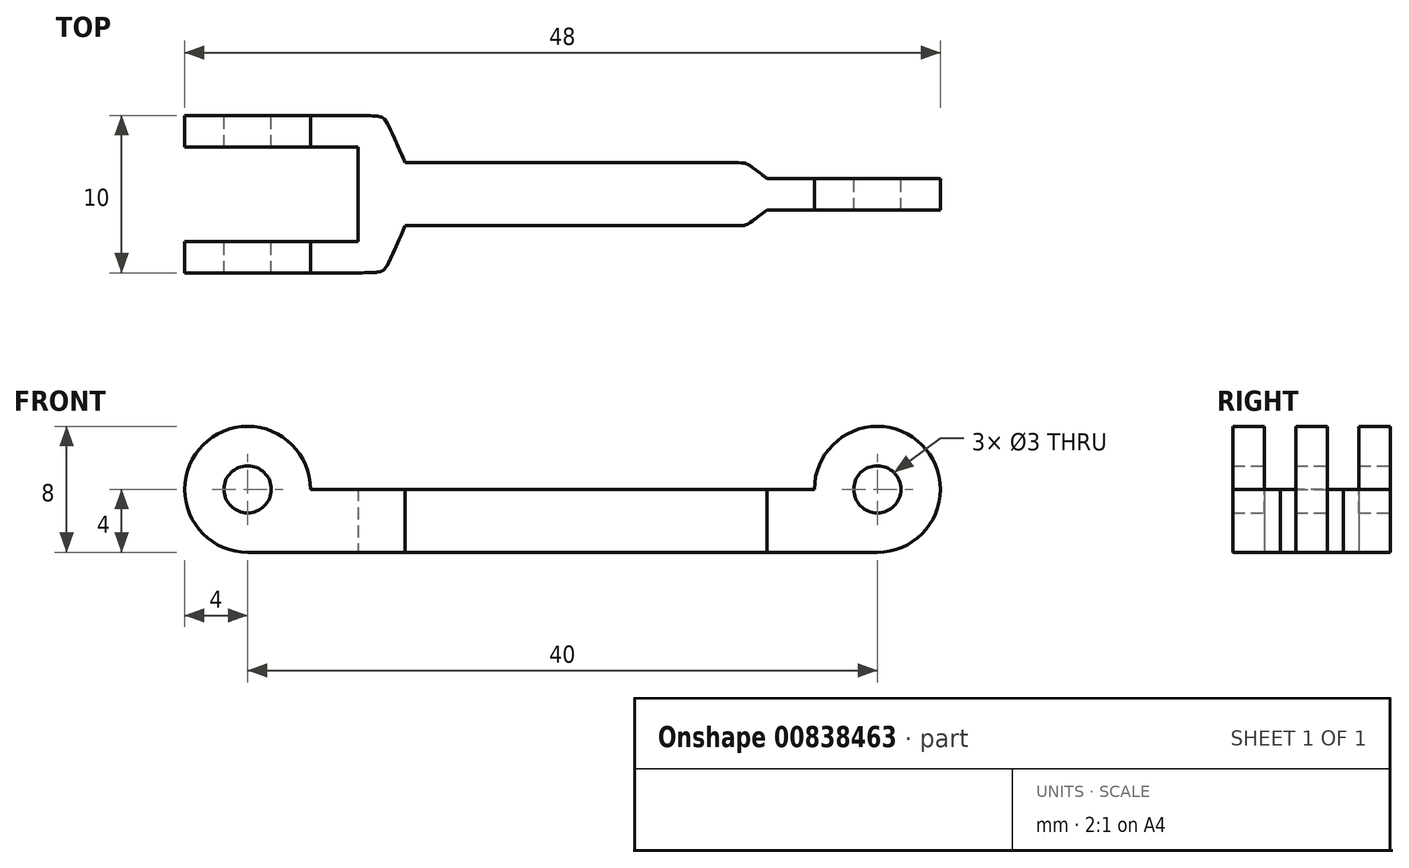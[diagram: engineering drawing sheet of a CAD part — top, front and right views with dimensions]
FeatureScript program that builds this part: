
annotation { "Feature Type Name" : "Feature", "Feature Type Description" : "" }
export const myFeature = defineFeature(function(context is Context, id is Id, definition is map)
    precondition{}
    {
        {
            var Q0;
            Q0=qCreatedBy(makeId("Front.planeOp"),FACE);
            var sketch = newSketch(context, id + "F0", { "sketchPlane" : qUnion([Q0])});
            skLineSegment(sketch, "E0.bottom", {"start": v(20, 2) * mm, "end": v(-20, 2) * mm});
            skLineSegment(sketch, "E0.top", {"start": v(20, -2) * mm, "end": v(-20, -2) * mm});
            skLineSegment(sketch, "E0.left", {"start": v(20, 2) * mm, "end": v(20, -2) * mm});
            skLineSegment(sketch, "E0.right", {"start": v(-20, 2) * mm, "end": v(-20, -2) * mm});
            skPoint(sketch, "E0.middle", {"position": v(0, 0) * mm});
            skLineSegment(sketch, "E1", {"start": v(-13, 2) * mm, "end": v(-13, -2) * mm});
            skLineSegment(sketch, "E2", {"start": v(-10, 2) * mm, "end": v(-10, -2) * mm});
            skCircle(sketch, "E3", {"center": v(20, 2) * mm, "radius": 4 * mm});
            skCircle(sketch, "E4", {"center": v(-20, 2) * mm, "radius": 4 * mm});
            skCircle(sketch, "E5", {"center": v(20, 2) * mm, "radius": 1.5 * mm});
            skCircle(sketch, "E6", {"center": v(-20, 2) * mm, "radius": 1.5 * mm});
            skLineSegment(sketch, "E7", {"start": v(13, 2) * mm, "end": v(13, -2) * mm});
            skSolve(sketch);
        }
        {
            var Q0;
            {var subQ0=sQuery(id+"F0.wireOp",EDGE,"E4");var subQ1=sQuery(id+"F0.wireOp",EDGE,"E0.bottom");var subQ2=makeQuery(id+"F0.imprint","INTERSECT",VERTEX,{"derivedFrom":[subQ1,subQ0]});Q0=makeQuery(id+"F0.imprint","IMPRINT",FACE,{"disambiguationData":[TD([[makeQuery(id+"F0.imprint","IMPRINT",EDGE,{"disambiguationData":[TD([[subQ2,-1.0]])],"derivedFrom":subQ1}),-1.0]])]});}
            var Q1;
            {var subQ0=sQuery(id+"F0.wireOp",EDGE,"E4");var subQ1=sQuery(id+"F0.wireOp",EDGE,"E0.bottom");var subQ2=makeQuery(id+"F0.imprint","INTERSECT",VERTEX,{"derivedFrom":[subQ1,subQ0]});Q1=makeQuery(id+"F0.imprint","IMPRINT",FACE,{"disambiguationData":[TD([[makeQuery(id+"F0.imprint","IMPRINT",EDGE,{"disambiguationData":[TD([[subQ2,-1.0]])],"derivedFrom":subQ1}),1.0]])]});}
            var Q2;
            {var subQ0=sQuery(id+"F0.wireOp",EDGE,"E1");Q2=makeQuery(id+"F0.imprint","IMPRINT",FACE,{"disambiguationData":[TD([[makeQuery(id+"F0.imprint","IMPRINT",EDGE,{"derivedFrom":subQ0}),-1.0]])]});}
            var Q3;
            {var subQ0=sQuery(id+"F0.wireOp",EDGE,"E1");Q3=makeQuery(id+"F0.imprint","IMPRINT",FACE,{"disambiguationData":[TD([[makeQuery(id+"F0.imprint","IMPRINT",EDGE,{"derivedFrom":subQ0}),1.0]])]});}
            extrude(context, id + "F1", {"entities" : qUnion([Q0, Q1, Q2, Q3]), "depth" : 10 * mm, "offsetDistance" : 25 * mm, "symmetric" : true});
        }
        {
            var Q0;
            {var subQ0=sQuery(id+"F0.wireOp",EDGE,"E2");Q0=makeQuery(id+"F0.imprint","IMPRINT",FACE,{"disambiguationData":[TD([[makeQuery(id+"F0.imprint","IMPRINT",EDGE,{"derivedFrom":subQ0}),1.0]])]});}
            extrude(context, id + "F2", {"entities" : qUnion([Q0]), "operationType" : NewBodyOperationType.ADD, "depth" : 4 * mm, "offsetDistance" : 25 * mm, "symmetric" : true});
        }
        {
            var Q0;
            {var subQ0=sQuery(id+"F0.wireOp",EDGE,"E7");Q0=makeQuery(id+"F0.imprint","IMPRINT",FACE,{"disambiguationData":[TD([[makeQuery(id+"F0.imprint","IMPRINT",EDGE,{"derivedFrom":subQ0}),1.0]])]});}
            var Q1;
            {var subQ0=sQuery(id+"F0.wireOp",EDGE,"E3");var subQ1=sQuery(id+"F0.wireOp",EDGE,"E0.bottom");var subQ2=makeQuery(id+"F0.imprint","INTERSECT",VERTEX,{"derivedFrom":[subQ1,subQ0]});Q1=makeQuery(id+"F0.imprint","IMPRINT",FACE,{"disambiguationData":[TD([[makeQuery(id+"F0.imprint","IMPRINT",EDGE,{"disambiguationData":[TD([[subQ2,1.0]])],"derivedFrom":subQ1}),1.0]])]});}
            var Q2;
            {var subQ0=sQuery(id+"F0.wireOp",EDGE,"E3");var subQ1=sQuery(id+"F0.wireOp",EDGE,"E0.bottom");var subQ2=makeQuery(id+"F0.imprint","INTERSECT",VERTEX,{"derivedFrom":[subQ1,subQ0]});Q2=makeQuery(id+"F0.imprint","IMPRINT",FACE,{"disambiguationData":[TD([[makeQuery(id+"F0.imprint","IMPRINT",EDGE,{"disambiguationData":[TD([[subQ2,1.0]])],"derivedFrom":subQ1}),-1.0]])]});}
            extrude(context, id + "F3", {"entities" : qUnion([Q0, Q1, Q2]), "operationType" : NewBodyOperationType.ADD, "depth" : 2 * mm, "offsetDistance" : 25 * mm, "symmetric" : true});
        }
        {
            var Q0;
            {var subQ0=sQuery(id+"F0.wireOp",EDGE,"E1");Q0=makeQuery(id+"F0.imprint","IMPRINT",FACE,{"disambiguationData":[TD([[makeQuery(id+"F0.imprint","IMPRINT",EDGE,{"derivedFrom":subQ0}),-1.0]])]});}
            var Q1;
            {var subQ0=sQuery(id+"F0.wireOp",EDGE,"E4");var subQ1=sQuery(id+"F0.wireOp",EDGE,"E0.bottom");var subQ2=makeQuery(id+"F0.imprint","INTERSECT",VERTEX,{"derivedFrom":[subQ1,subQ0]});Q1=makeQuery(id+"F0.imprint","IMPRINT",FACE,{"disambiguationData":[TD([[makeQuery(id+"F0.imprint","IMPRINT",EDGE,{"disambiguationData":[TD([[subQ2,-1.0]])],"derivedFrom":subQ1}),1.0]])]});}
            var Q2;
            {var subQ0=sQuery(id+"F0.wireOp",EDGE,"E4");var subQ1=sQuery(id+"F0.wireOp",EDGE,"E0.bottom");var subQ2=makeQuery(id+"F0.imprint","INTERSECT",VERTEX,{"derivedFrom":[subQ1,subQ0]});Q2=makeQuery(id+"F0.imprint","IMPRINT",FACE,{"disambiguationData":[TD([[makeQuery(id+"F0.imprint","IMPRINT",EDGE,{"disambiguationData":[TD([[subQ2,-1.0]])],"derivedFrom":subQ1}),-1.0]])]});}
            extrude(context, id + "F4", {"entities" : qUnion([Q0, Q1, Q2]), "operationType" : NewBodyOperationType.REMOVE, "oppositeDirection" : true, "depth" : 6 * mm, "offsetDistance" : 25 * mm, "symmetric" : true});
        }
        {
            var Q0;
            Q0=makeQuery(id+"F1.opExtrude","CAP_EDGE",EDGE,{"disambiguationData":[OSD([sQuery(id+"F0.wireOp",EDGE,"E2")])],"isStart":false});
            var Q1;
            Q1=makeQuery(id+"F2.opExtrude","CAP_EDGE",EDGE,{"disambiguationData":[OSD([sQuery(id+"F0.wireOp",EDGE,"E7")])],"isStart":false});
            var Q2;
            Q2=makeQuery(id+"F1.opExtrude","CAP_EDGE",EDGE,{"disambiguationData":[OSD([sQuery(id+"F0.wireOp",EDGE,"E2")])],"isStart":true});
            var Q3;
            Q3=makeQuery(id+"F2.opExtrude","CAP_EDGE",EDGE,{"disambiguationData":[OSD([sQuery(id+"F0.wireOp",EDGE,"E7")])],"isStart":true});
            fillet(context, id + "F5", {"entities" : qUnion([Q0, Q1, Q2, Q3]), "radius" : 5 * mm, "tangentPropagation" : true, "rho" : 0.9, "crossSection" : FilletCrossSection.CONIC, "allowEdgeOverflow" : false});
        }
    });
